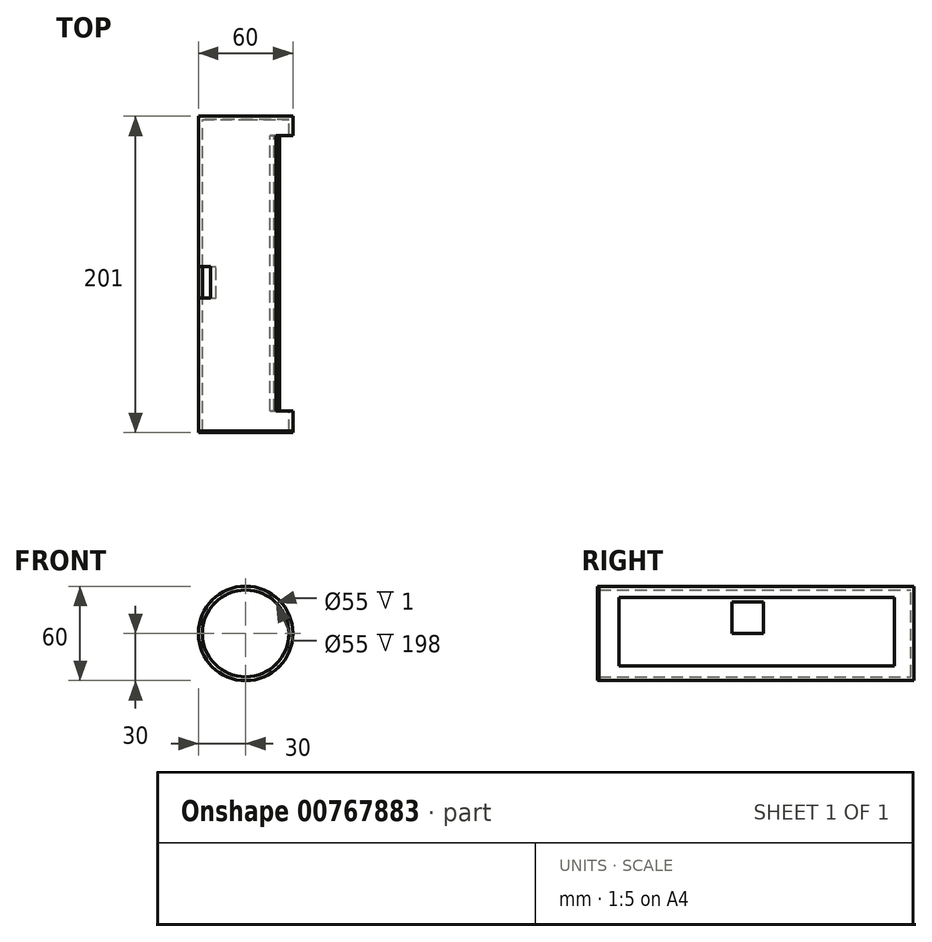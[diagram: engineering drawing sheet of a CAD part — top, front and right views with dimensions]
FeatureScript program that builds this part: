
annotation { "Feature Type Name" : "Feature", "Feature Type Description" : "" }
export const myFeature = defineFeature(function(context is Context, id is Id, definition is map)
    precondition{}
    {
        {
            var Q0;
            Q0=qCreatedBy(makeId("Front.planeOp"),FACE);
            var sketch = newSketch(context, id + "F0", { "sketchPlane" : qUnion([Q0])});
            skCircle(sketch, "E0", {"center": v(0, 0) * mm, "radius": 30 * mm});
            skSolve(sketch);
        }
        {
            var Q0;
            Q0=makeQuery(id+"F0.imprint","IMPRINT",FACE,{"disambiguationData":[TD([[makeQuery(id+"F0.imprint","IMPRINT",EDGE,{"derivedFrom":sQuery(id+"F0.wireOp",EDGE,"E0")}),1.0]])]});
            extrude(context, id + "F1", {"entities" : qUnion([Q0]), "depth" : 200 * mm, "offsetDistance" : 25 * mm});
        }
        {
            var Q0;
            Q0=makeQuery(id+"F1.opExtrude","CAP_FACE",FACE,{"disambiguationData":[OSD([sQuery(id+"F0.wireOp",EDGE,"E0")])],"isStart":true});
            var sketch = newSketch(context, id + "F2", { "sketchPlane" : qUnion([Q0])});
            skCircle(sketch, "E1", {"center": v(0, 0) * mm, "radius": 27.5 * mm});
            skSolve(sketch);
        }
        {
            var Q0;
            Q0=makeQuery(id+"F2.imprint","IMPRINT",FACE,{"disambiguationData":[TD([[makeQuery(id+"F2.imprint","IMPRINT",EDGE,{"derivedFrom":sQuery(id+"F2.wireOp",EDGE,"E1")}),1.0]])]});
            extrude(context, id + "F3", {"entities" : qUnion([Q0]), "operationType" : NewBodyOperationType.REMOVE, "endBound" : BoundingType.UP_TO_NEXT, "oppositeDirection" : true, "depth" : 25 * mm, "offsetDistance" : 25 * mm});
        }
        {
            var Q0;
            Q0=qCreatedBy(makeId("Front.planeOp"),FACE);
            var sketch = newSketch(context, id + "F4", { "sketchPlane" : qUnion([Q0])});
            skCircle(sketch, "E2", {"center": v(0, 0) * mm, "radius": 30 * mm});
            skSolve(sketch);
        }
        {
            var Q0;
            Q0=makeQuery(id+"F4.imprint","IMPRINT",FACE,{"disambiguationData":[TD([[makeQuery(id+"F4.imprint","IMPRINT",EDGE,{"derivedFrom":sQuery(id+"F4.wireOp",EDGE,"E2")}),1.0]])]});
            extrude(context, id + "F5", {"entities" : qUnion([Q0]), "operationType" : NewBodyOperationType.ADD, "depth" : 2 * mm, "offsetDistance" : 25 * mm});
        }
        {
            var Q0;
            Q0=makeQuery(id+"F1.opExtrude","CAP_FACE",FACE,{"disambiguationData":[OSD([sQuery(id+"F0.wireOp",EDGE,"E0")])],"isStart":false});
            var sketch = newSketch(context, id + "F6", { "sketchPlane" : qUnion([Q0])});
            skCircle(sketch, "E3", {"center": v(0, 0) * mm, "radius": 30 * mm});
            skSolve(sketch);
        }
        {
            var Q0;
            Q0=makeQuery(id+"F6.imprint","IMPRINT",FACE,{"disambiguationData":[TD([[makeQuery(id+"F6.imprint","IMPRINT",EDGE,{"derivedFrom":sQuery(id+"F6.wireOp",EDGE,"E3")}),1.0]])]});
            var Q1;
            Q1=makeQuery(id+"F6.imprint","IMPRINT",FACE,{"disambiguationData":[TD([[makeQuery(id+"F6.imprint","IMPRINT",EDGE,{"derivedFrom":makeQuery(id+"F3.boolean.opBoolean","COPY",EDGE,{"derivedFrom":makeQuery(id+"F3.opExtrude","CAP_EDGE",EDGE,{"disambiguationData":[OSD([sQuery(id+"F2.wireOp",EDGE,"E1")])],"isStart":false})})}),-1.0]])]});
            extrude(context, id + "F7", {"entities" : qUnion([Q0, Q1]), "depth" : 1 * mm, "offsetDistance" : 25 * mm});
        }
        {
            var Q0;
            Q0=qCreatedBy(makeId("Right.planeOp"),FACE);
            var sketch = newSketch(context, id + "F8", { "sketchPlane" : qUnion([Q0])});
            skLineSegment(sketch, "E4.bottom", {"start": v(-95.45, 0) * mm, "end": v(-115.45, 0) * mm});
            skLineSegment(sketch, "E4.top", {"start": v(-95.45, 20) * mm, "end": v(-115.45, 20) * mm});
            skLineSegment(sketch, "E4.left", {"start": v(-95.45, 0) * mm, "end": v(-95.45, 20) * mm});
            skLineSegment(sketch, "E4.right", {"start": v(-115.45, 0) * mm, "end": v(-115.45, 20) * mm});
            skSolve(sketch);
        }
        {
            var Q0;
            Q0=makeQuery(id+"F8.imprint","IMPRINT",FACE,{"disambiguationData":[TD([[makeQuery(id+"F8.imprint","IMPRINT",EDGE,{"derivedFrom":sQuery(id+"F8.wireOp",EDGE,"E4.bottom")}),-1.0]])]});
            extrude(context, id + "F9", {"entities" : qUnion([Q0]), "operationType" : NewBodyOperationType.REMOVE, "oppositeDirection" : true, "depth" : 67.5 * mm, "offsetDistance" : 25 * mm});
        }
        {
            var Q0;
            Q0=qCreatedBy(makeId("Right.planeOp"),FACE);
            var sketch = newSketch(context, id + "F10", { "sketchPlane" : qUnion([Q0])});
            skLineSegment(sketch, "E5.bottom", {"start": v(-187.24, 22.82) * mm, "end": v(-12.3, 22.82) * mm});
            skLineSegment(sketch, "E5.top", {"start": v(-187.24, -20.78) * mm, "end": v(-12.3, -20.78) * mm});
            skLineSegment(sketch, "E5.left", {"start": v(-187.24, 22.82) * mm, "end": v(-187.24, -20.78) * mm});
            skLineSegment(sketch, "E5.right", {"start": v(-12.3, 22.82) * mm, "end": v(-12.3, -20.78) * mm});
            skSolve(sketch);
        }
        {
            var Q0;
            Q0 = qSketchRegion(id + "F10", true);
            extrude(context, id + "F11", {"entities" : qUnion([Q0]), "operationType" : NewBodyOperationType.REMOVE, "depth" : 173 * mm, "offsetDistance" : 25 * mm});
        }
    });
